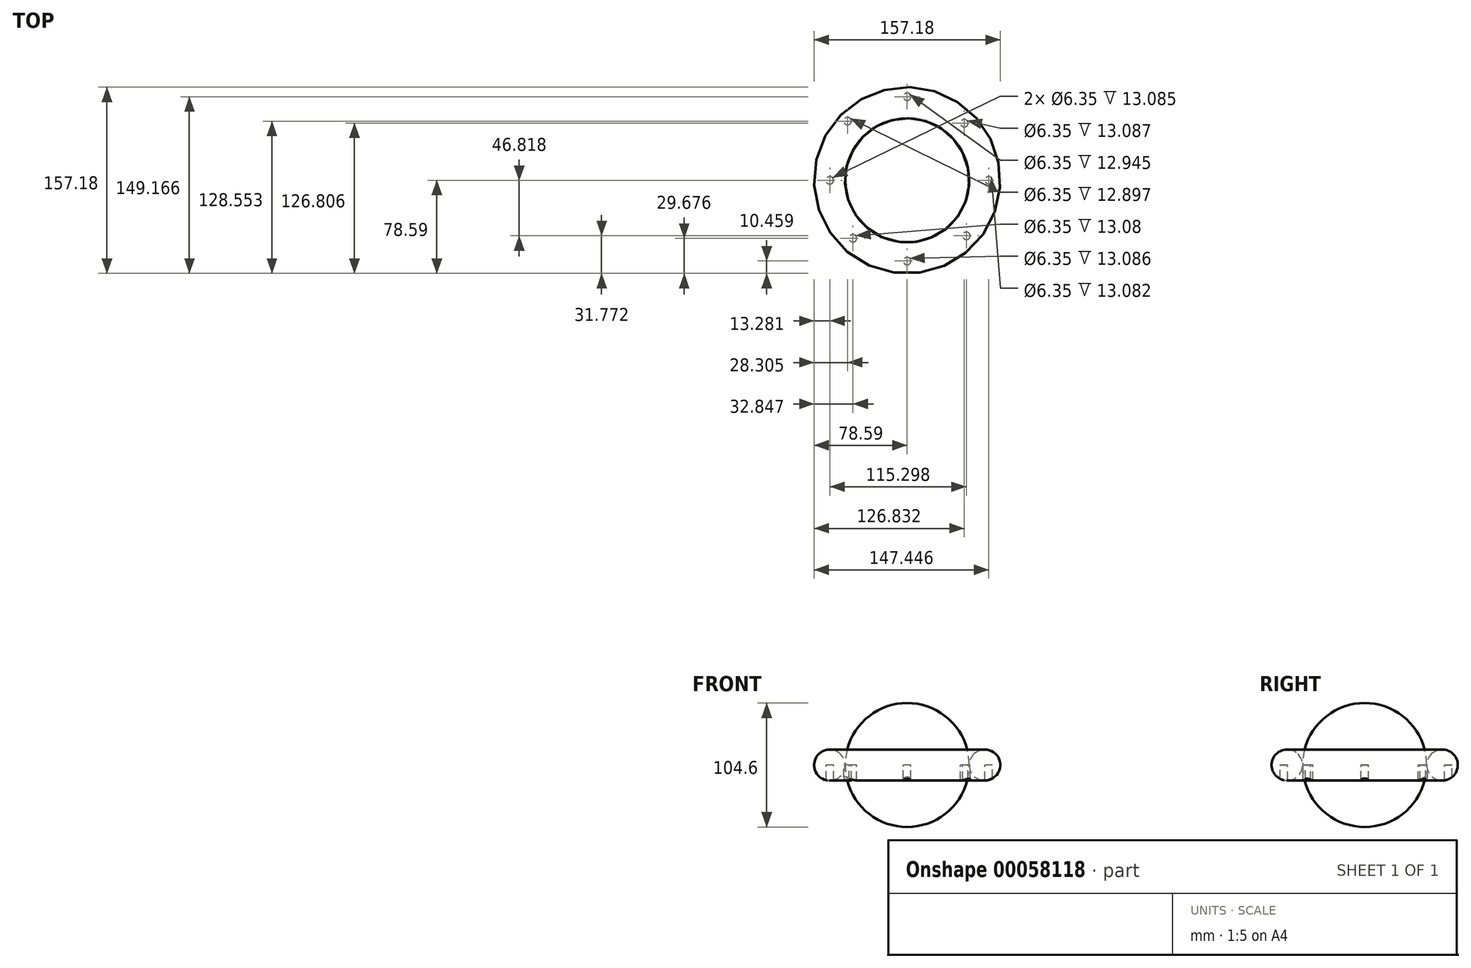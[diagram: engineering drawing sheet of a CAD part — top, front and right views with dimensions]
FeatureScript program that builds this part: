
annotation { "Feature Type Name" : "Feature", "Feature Type Description" : "" }
export const myFeature = defineFeature(function(context is Context, id is Id, definition is map)
    precondition{}
    {
        {
            var Q0;
            Q0=qCreatedBy(makeId("Front.planeOp"),FACE);
            var sketch = newSketch(context, id + "F0", { "sketchPlane" : qUnion([Q0])});
            skCircle(sketch, "E0", {"center": v(-65.51, 0) * mm, "radius": 13.08 * mm});
            skLineSegment(sketch, "E1", {"start": v(0, 33.54) * mm, "end": v(0, -42.97) * mm});
            skSolve(sketch);
        }
        {
            var Q0;
            Q0=makeQuery(id+"F0.imprint","IMPRINT",FACE,{"disambiguationData":[TD([[makeQuery(id+"F0.imprint","IMPRINT",EDGE,{"derivedFrom":sQuery(id+"F0.wireOp",EDGE,"E0")}),1.0]])]});
            var Q1;
            Q1=sQuery(id+"F0.wireOp",EDGE,"E1");
            revolve(context, id + "F1", {"entities" : qUnion([Q0]), "axis" : qUnion([Q1]), "revolveType" : RevolveType.FULL});
        }
        {
            var Q0;
            Q0=qCreatedBy(makeId("Top.planeOp"),FACE);
            var sketch = newSketch(context, id + "F2", { "sketchPlane" : qUnion([Q0])});
            skCircle(sketch, "E2", {"center": v(0, 0) * mm, "radius": 52.3 * mm});
            skLineSegment(sketch, "E3", {"start": v(0, 52.3) * mm, "end": v(0, -52.3) * mm});
            skSolve(sketch);
        }
        {
            var Q0;
            {var subQ0=sQuery(id+"F2.wireOp",EDGE,"E3");Q0=makeQuery(id+"F2.imprint","IMPRINT",FACE,{"disambiguationData":[TD([[makeQuery(id+"F2.imprint","IMPRINT",EDGE,{"derivedFrom":subQ0}),-1.0]])]});}
            var Q1;
            Q1=sQuery(id+"F2.wireOp",EDGE,"E3");
            revolve(context, id + "F3", {"entities" : qUnion([Q0]), "axis" : qUnion([Q1]), "revolveType" : RevolveType.FULL});
        }
        {
            var Q0;
            Q0=qCreatedBy(makeId("Top.planeOp"),FACE);
            var sketch = newSketch(context, id + "F4", { "sketchPlane" : qUnion([Q0])});
            skLineSegment(sketch, "E4", {"start": v(-50.29, 49.96) * mm, "end": v(0, 70.58) * mm});
            skLineSegment(sketch, "E5", {"start": v(0, 70.58) * mm, "end": v(48.24, 48.22) * mm});
            skLineSegment(sketch, "E6", {"start": v(48.24, 48.22) * mm, "end": v(68.86, 0) * mm});
            skLineSegment(sketch, "E7", {"start": v(68.86, 0) * mm, "end": v(49.99, -46.82) * mm});
            skLineSegment(sketch, "E8", {"start": v(49.99, -46.82) * mm, "end": v(0, -68.13) * mm});
            skLineSegment(sketch, "E9", {"start": v(0, -68.13) * mm, "end": v(-45.74, -48.91) * mm});
            skLineSegment(sketch, "E10", {"start": v(-45.74, -48.91) * mm, "end": v(-65.3, 0) * mm});
            skLineSegment(sketch, "E11", {"start": v(-65.3, 0) * mm, "end": v(-50.29, 49.96) * mm});
            skSolve(sketch);
        }
        {
            var Q0;
            Q0=sQuery(id+"F4.wireOp",VERTEX,"E7.start");
            var Q1;
            Q1=sQuery(id+"F4.wireOp",VERTEX,"E8.start");
            var Q2;
            Q2=sQuery(id+"F4.wireOp",VERTEX,"E9.start");
            var Q3;
            Q3=sQuery(id+"F4.wireOp",VERTEX,"E10.start");
            var Q4;
            Q4=sQuery(id+"F4.wireOp",VERTEX,"E11.start");
            var Q5;
            Q5=sQuery(id+"F4.wireOp",VERTEX,"E11.end");
            var Q6;
            Q6=sQuery(id+"F4.wireOp",VERTEX,"E5.start");
            var Q7;
            Q7=sQuery(id+"F4.wireOp",VERTEX,"E6.start");
            var Q8;
            Q8=makeQuery(id+"F1.opRevolve","SWEPT_BODY",BODY,{"disambiguationData":[OSD([sQuery(id+"F0.wireOp",EDGE,"E0")])]});
            hole(context, id + "F5", {"style" : HoleStyle.SIMPLE, "holeDiameter" : 6.35 * mm, "endStyle" : HoleEndStyle.THROUGH, "locations" : qUnion([Q0, Q1, Q2, Q3, Q4, Q5, Q6, Q7]), "scope" : qUnion([Q8])});
        }
    });
